# Revit family: 9. Секция роторного регенератора ANR R2
name_source: partatom
category: Оборудование
revit_build: Autodesk Revit 2016 (Build: 20161004_0715(x64)
units: mm (PartAtom-declared; Revit-internal decimal feet)

## family parameters
Всегда вертикально = Да
На основе рабочей плоскости = Нет
Общий = Нет
При загрузке вырезать с полостями = Нет
Размер круглого соединителя = Использовать диаметр
Тип детали = Нормальный
Точка расчета площади = Нет

## types (6) — shared parameters
h = 180 мм
Единица измерения = шт.
Завод изготовитель = KORF
Ключевая пометка = Вентиляция
Материал = Сталь серая
Наименование и тех.хар-ка = Секция роторного регенератора
Раздел = ОВ
Синий = Синий
высота ножек = 170 мм

## per-type parameters (varying)
| type | А | А1 | Б | Б1 | Высота | Д | Д патрубков | Д1 | Ж | З | Заправочный объем, л | И | И1 | К | К1 | К2 | К5 | Середина | Ширина |
| ANR 20 R2 | 2610 мм | 2590 мм | 3273 мм | 3253 мм | 3198 мм | 1100 мм | 28 мм | 1080 мм | 813 мм | 157 мм | 7 м³ | 473 мм | 236 мм | 227 мм | 454 мм | 173 мм | 313 мм | 1807 мм | 2535 мм |
| ANR 25 R2 | 3005 мм | 2985 мм | 4043 мм | 4023 мм | 3968 мм | 1100 мм | 28 мм | 1080 мм | 1006 мм | 157 мм | 37.8 м³ | 473 мм | 236 мм | 227 мм | 454 мм | 173 мм | 313 мм | 2192 мм | 2930 мм |
| ANR 7 R2 | 1825 мм | 1805 мм | 2593 мм | 2573 мм | 2518 мм | 980 мм | 40 мм | 960 мм | 643 мм | 140 мм | 14.3 м³ | 763 мм | 382 мм | 202 мм | 403 мм | 154 мм | 278 мм | 1467 мм | 1750 мм |
| ANR 8 R2 | 1975 мм | 1955 мм | 2593 мм | 2573 мм | 2518 мм | 840 мм | 40 мм | 820 мм | 643 мм | 120 мм | 19.3 м³ | 473 мм | 236 мм | 172 мм | 344 мм | 131 мм | 238 мм | 1467 мм | 1900 мм |
| ANR 6 R2 | 1615 мм | 1595 мм | 2153 мм | 2133 мм | 2078 мм | 680 мм | 28 мм | 660 мм | 533 мм | 97 мм | 7 м³ | 473 мм | 236 мм | 139 мм | 277 мм | 106 мм | 191 мм | 1247 мм | 1540 мм |
| ANR 12 R2 | 2255 мм | 2235 мм | 2823 мм | 2803 мм | 2748 мм | 980 мм | 35 мм | 960 мм | 701 мм | 140 мм | 13.3 м³ | 473 мм | 236 мм | 202 мм | 403 мм | 154 мм | 278 мм | 1582 мм | 2180 мм |

note: column(s) folded — value = type name in every type: Тип, марка, обозначение
